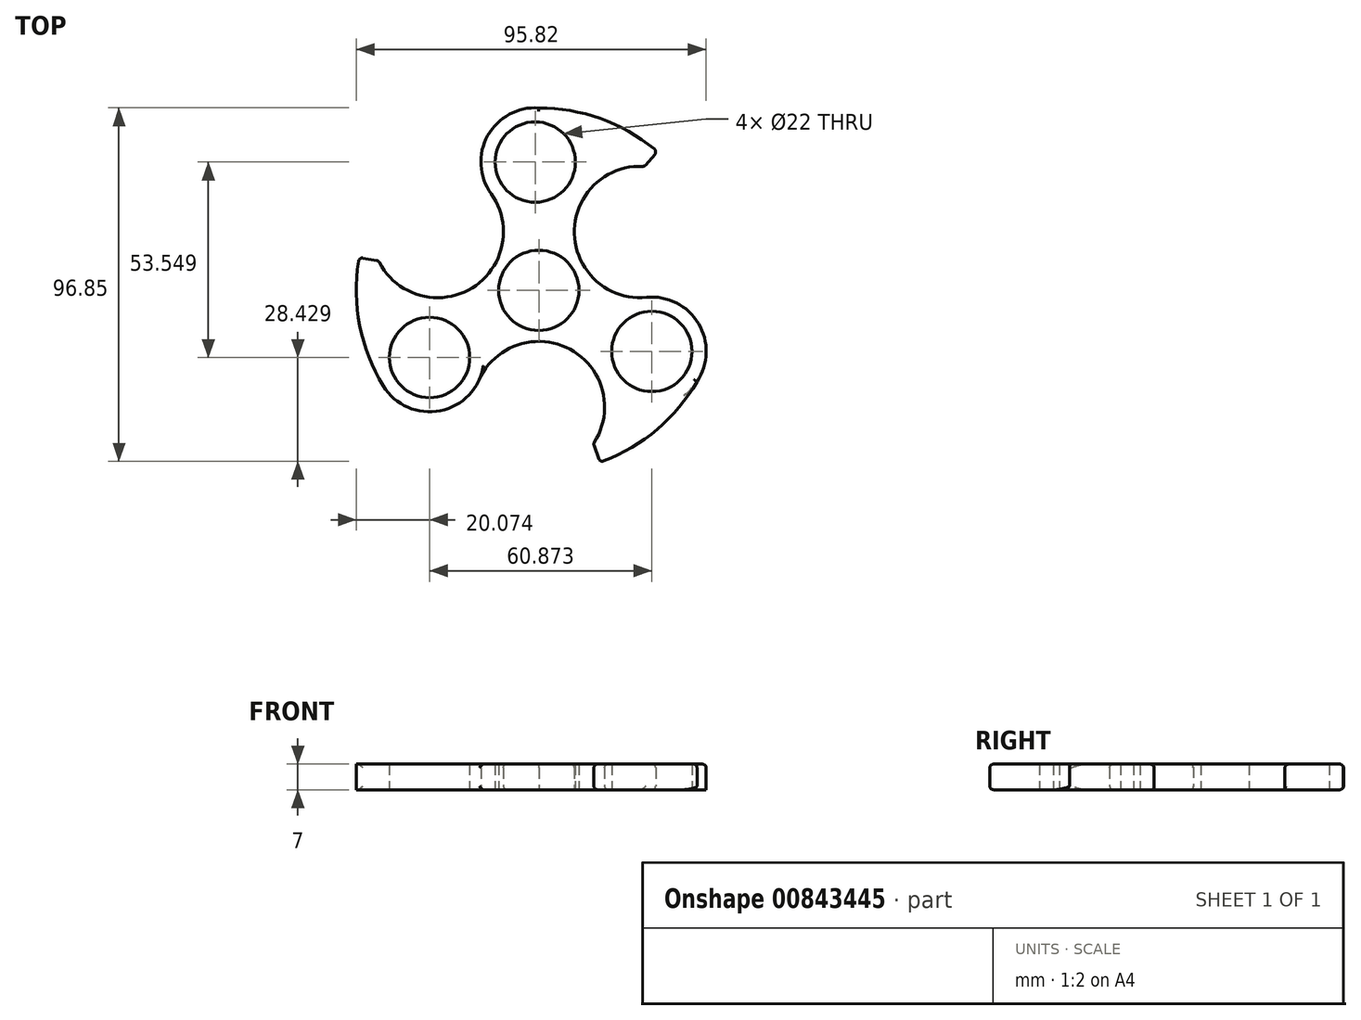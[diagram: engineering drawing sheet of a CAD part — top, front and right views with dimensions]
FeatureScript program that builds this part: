
annotation { "Feature Type Name" : "Feature", "Feature Type Description" : "" }
export const myFeature = defineFeature(function(context is Context, id is Id, definition is map)
    precondition{}
    {
        {
            var Q0;
            Q0=qCreatedBy(makeId("Top.planeOp"),FACE);
            var sketch = newSketch(context, id + "F0", { "sketchPlane" : qUnion([Q0])});
            skCircle(sketch, "E0", {"center": v(0, 0) * mm, "radius": 11 * mm});
            skArc(sketch, "E1", {"start": v(-49.18, 9.03) * mm, "mid": v(-49.15, -9.18) * mm, "end": v(-42.6, -26.18) * mm});
            skArc(sketch, "E2", {"start": v(-43.87, 8.06) * mm, "mid": v(-18.47, 0.56) * mm, "end": v(-13.09, 26.49) * mm});
            skArc(sketch, "E3", {"start": v(28.91, 33.96) * mm, "mid": v(9.72, 15.71) * mm, "end": v(29.48, -1.91) * mm});
            skArc(sketch, "E4", {"start": v(14.95, -42.02) * mm, "mid": v(8.77, -16.28) * mm, "end": v(-16.38, -24.53) * mm});
            skArc(sketch, "E5.trimOffspring", {"start": v(16.76, -47.1) * mm, "mid": v(32, -38.42) * mm, "end": v(43.3, -25) * mm});
            skArc(sketch, "E6.trimOffspring", {"start": v(32.41, 38.07) * mm, "mid": v(17.27, 46.92) * mm, "end": v(0, 50) * mm});
            skPoint(sketch, "E7", {"position": v(23.2, 38.55) * mm});
            skPoint(sketch, "E8", {"position": v(21.79, -39.38) * mm});
            skPoint(sketch, "E9", {"position": v(-45, 0.82) * mm});
            skArc(sketch, "E10", {"start": v(-13.09, 26.49) * mm, "mid": v(-14, 42.4) * mm, "end": v(0, 50) * mm});
            skArc(sketch, "E11", {"start": v(-42.6, -26.18) * mm, "mid": v(-29, -33.24) * mm, "end": v(-16.38, -24.53) * mm});
            skArc(sketch, "E12", {"start": v(29.48, -1.91) * mm, "mid": v(43.71, -9.08) * mm, "end": v(43.3, -25) * mm});
            skCircle(sketch, "E13", {"center": v(-29.93, -18.4) * mm, "radius": 11 * mm});
            skCircle(sketch, "E14", {"center": v(-1, 35.16) * mm, "radius": 11 * mm});
            skCircle(sketch, "E15", {"center": v(30.95, -16.72) * mm, "radius": 11 * mm});
            skLineSegment(sketch, "E16", {"start": v(0, 0) * mm, "end": v(37.87, 44.49) * mm, "construction": true});
            skLineSegment(sketch, "E17.1.0", {"start": v(0, 0) * mm, "end": v(-57.46, 10.56) * mm, "construction": true});
            skLineSegment(sketch, "E17.2.0", {"start": v(0, 0) * mm, "end": v(19.59, -55.04) * mm, "construction": true});
            skLineSegment(sketch, "E18", {"start": v(-49.18, 9.03) * mm, "end": v(-43.87, 8.06) * mm});
            skLineSegment(sketch, "E19", {"start": v(14.95, -42.02) * mm, "end": v(16.76, -47.1) * mm});
            skLineSegment(sketch, "E20", {"start": v(32.41, 38.07) * mm, "end": v(28.91, 33.96) * mm});
            skSolve(sketch);
        }
        {
            var Q0;
            {var subQ1=sQuery(id+"F0.wireOp",EDGE,"3f7bc842-8467-49ac-8440-9adaad4e2810.2");Q0=makeQuery(id+"F0.imprint","IMPRINT",FACE,{"disambiguationData":[TD([[makeQuery(id+"F0.imprint","IMPRINT",EDGE,{"derivedFrom":subQ1}),1.0]])]});}
            var Q1;
            {var subQ5=sQuery(id+"F0.wireOp",EDGE,"3f7bc842-8467-49ac-8440-9adaad4e2810.0");Q1=makeQuery(id+"F0.imprint","IMPRINT",FACE,{"disambiguationData":[TD([[makeQuery(id+"F0.imprint","IMPRINT",EDGE,{"derivedFrom":subQ5}),1.0]])]});}
            var Q2;
            {var subQ0=sQuery(id+"F0.wireOp",EDGE,"3f7bc842-8467-49ac-8440-9adaad4e2810.1");var subQ1=sQuery(id+"F0.wireOp",EDGE,"nu7MbhjY-MAc7-rPjX-g1DX-lD3kLk05fhsn");var subQ2=makeQuery(id+"F0.imprint","INTERSECT",VERTEX,{"derivedFrom":[subQ1,subQ0]});Q2=makeQuery(id+"F0.imprint","IMPRINT",FACE,{"disambiguationData":[TD([[makeQuery(id+"F0.imprint","IMPRINT",EDGE,{"disambiguationData":[TD([[subQ2,1.0]])],"derivedFrom":subQ0}),1.0]])]});}
            var Q3;
            {var subQ0=sQuery(id+"F0.wireOp",EDGE,"3f7bc842-8467-49ac-8440-9adaad4e2810.1");var subQ1=sQuery(id+"F0.wireOp",EDGE,"nu7MbhjY-MAc7-rPjX-g1DX-lD3kLk05fhsn");var subQ2=makeQuery(id+"F0.imprint","INTERSECT",VERTEX,{"derivedFrom":[subQ1,subQ0]});Q3=makeQuery(id+"F0.imprint","IMPRINT",FACE,{"disambiguationData":[TD([[makeQuery(id+"F0.imprint","IMPRINT",EDGE,{"disambiguationData":[TD([[subQ2,-1.0]])],"derivedFrom":subQ0}),1.0]])]});}
            var Q4;
            {var subQ0=sQuery(id+"F0.wireOp",EDGE,"E2");var subQ1=sQuery(id+"F0.wireOp",EDGE,"sv7fbsnc-qcye-DYNE-iSqw-857IQjWxAevf");var subQ2=makeQuery(id+"F0.imprint","INTERSECT",VERTEX,{"derivedFrom":[subQ1,subQ0]});Q4=makeQuery(id+"F0.imprint","IMPRINT",FACE,{"disambiguationData":[TD([[makeQuery(id+"F0.imprint","IMPRINT",EDGE,{"disambiguationData":[TD([[subQ2,-1.0]])],"derivedFrom":subQ1}),-1.0]])]});}
            var Q5;
            {var subQ0=sQuery(id+"F0.wireOp",EDGE,"E3");var subQ1=sQuery(id+"F0.wireOp",EDGE,"sv7fbsnc-qcye-DYNE-iSqw-857IQjWxAevf");var subQ2=makeQuery(id+"F0.imprint","INTERSECT",VERTEX,{"derivedFrom":[subQ1,subQ0]});Q5=makeQuery(id+"F0.imprint","IMPRINT",FACE,{"disambiguationData":[TD([[makeQuery(id+"F0.imprint","IMPRINT",EDGE,{"disambiguationData":[TD([[subQ2,1.0]])],"derivedFrom":subQ1}),-1.0]])]});}
            var Q6;
            {var subQ3=sQuery(id+"F0.wireOp",EDGE,"E2");var subQ5=sQuery(id+"F0.wireOp",EDGE,"C4j8nSnC-YMSu-Lszk-EYxg-b8w5SDZCJpY5");var subQ6=makeQuery(id+"F0.imprint","INTERSECT",VERTEX,{"disambiguationData":[OD(0.0)],"derivedFrom":[subQ5,subQ3]});Q6=makeQuery(id+"F0.imprint","IMPRINT",FACE,{"disambiguationData":[TD([[makeQuery(id+"F0.imprint","IMPRINT",EDGE,{"disambiguationData":[TD([[subQ6,1.0]])],"derivedFrom":subQ5}),1.0]])]});}
            var Q7;
            {var subQ1=sQuery(id+"F0.wireOp",EDGE,"C4j8nSnC-YMSu-Lszk-EYxg-b8w5SDZCJpY5");var subQ7=sQuery(id+"F0.wireOp",EDGE,"E3");var subQ9=makeQuery(id+"F0.imprint","INTERSECT",VERTEX,{"disambiguationData":[OD(1.0)],"derivedFrom":[subQ1,subQ7]});Q7=makeQuery(id+"F0.imprint","IMPRINT",FACE,{"disambiguationData":[TD([[makeQuery(id+"F0.imprint","IMPRINT",EDGE,{"disambiguationData":[TD([[subQ9,-1.0]])],"derivedFrom":subQ1}),1.0]])]});}
            var Q8;
            {var subQ1=sQuery(id+"F0.wireOp",EDGE,"C4j8nSnC-YMSu-Lszk-EYxg-b8w5SDZCJpY5");var subQ5=sQuery(id+"F0.wireOp",EDGE,"E2");var subQ6=makeQuery(id+"F0.imprint","INTERSECT",VERTEX,{"disambiguationData":[OD(1.0)],"derivedFrom":[subQ1,subQ5]});Q8=makeQuery(id+"F0.imprint","IMPRINT",FACE,{"disambiguationData":[TD([[makeQuery(id+"F0.imprint","IMPRINT",EDGE,{"disambiguationData":[TD([[subQ6,-1.0]])],"derivedFrom":subQ1}),1.0]])]});}
            var Q9;
            {var subQ1=sQuery(id+"F0.wireOp",EDGE,"C4j8nSnC-YMSu-Lszk-EYxg-b8w5SDZCJpY5");var subQ5=sQuery(id+"F0.wireOp",EDGE,"E4");var subQ6=makeQuery(id+"F0.imprint","INTERSECT",VERTEX,{"disambiguationData":[OD(0.0)],"derivedFrom":[subQ1,subQ5]});Q9=makeQuery(id+"F0.imprint","IMPRINT",FACE,{"disambiguationData":[TD([[makeQuery(id+"F0.imprint","IMPRINT",EDGE,{"disambiguationData":[TD([[subQ6,1.0]])],"derivedFrom":subQ1}),1.0]])]});}
            var Q10;
            {var subQ5=sQuery(id+"F0.wireOp",EDGE,"9VgUR1kC-HbJB-ABtG-h0EX-FUHrEpssJFZg");var subQ6=sQuery(id+"F0.wireOp",EDGE,"E0");var subQ7=makeQuery(id+"F0.imprint","INTERSECT",VERTEX,{"derivedFrom":[subQ6,subQ5]});Q10=makeQuery(id+"F0.imprint","IMPRINT",FACE,{"disambiguationData":[TD([[makeQuery(id+"F0.imprint","IMPRINT",EDGE,{"disambiguationData":[TD([[subQ7,-1.0]])],"derivedFrom":subQ6}),-1.0]])]});}
            var Q11;
            {var subQ1=sQuery(id+"F0.wireOp",EDGE,"E0");var subQ9=sQuery(id+"F0.wireOp",EDGE,"CFaMabJv-BaBl-nt57-wO3A-6JOnLyDZJUd2");var subQ11=makeQuery(id+"F0.imprint","INTERSECT",VERTEX,{"derivedFrom":[subQ1,subQ9]});Q11=makeQuery(id+"F0.imprint","IMPRINT",FACE,{"disambiguationData":[TD([[makeQuery(id+"F0.imprint","IMPRINT",EDGE,{"disambiguationData":[TD([[subQ11,1.0]])],"derivedFrom":subQ1}),-1.0]])]});}
            var Q12;
            {var subQ0=sQuery(id+"F0.wireOp",EDGE,"E3");var subQ1=sQuery(id+"F0.wireOp",EDGE,"x40MpVTq-PCuQ-1TBw-DNN8-5xuqoy8G5yz2");var subQ2=makeQuery(id+"F0.imprint","INTERSECT",VERTEX,{"derivedFrom":[subQ1,subQ0]});Q12=makeQuery(id+"F0.imprint","IMPRINT",FACE,{"disambiguationData":[TD([[makeQuery(id+"F0.imprint","IMPRINT",EDGE,{"disambiguationData":[TD([[subQ2,-1.0]])],"derivedFrom":subQ1}),-1.0]])]});}
            var Q13;
            {var subQ0=sQuery(id+"F0.wireOp",EDGE,"E4");var subQ1=sQuery(id+"F0.wireOp",EDGE,"x40MpVTq-PCuQ-1TBw-DNN8-5xuqoy8G5yz2");var subQ2=makeQuery(id+"F0.imprint","INTERSECT",VERTEX,{"derivedFrom":[subQ1,subQ0]});Q13=makeQuery(id+"F0.imprint","IMPRINT",FACE,{"disambiguationData":[TD([[makeQuery(id+"F0.imprint","IMPRINT",EDGE,{"disambiguationData":[TD([[subQ2,1.0]])],"derivedFrom":subQ1}),-1.0]])]});}
            var Q14;
            {var subQ0=sQuery(id+"F0.wireOp",EDGE,"49722dc7-dc7b-4ebf-b22a-0d9910023828.2");Q14=makeQuery(id+"F0.imprint","IMPRINT",FACE,{"disambiguationData":[TD([[makeQuery(id+"F0.imprint","IMPRINT",EDGE,{"derivedFrom":subQ0}),1.0]])]});}
            var Q15;
            {var subQ5=sQuery(id+"F0.wireOp",EDGE,"49722dc7-dc7b-4ebf-b22a-0d9910023828.0");Q15=makeQuery(id+"F0.imprint","IMPRINT",FACE,{"disambiguationData":[TD([[makeQuery(id+"F0.imprint","IMPRINT",EDGE,{"derivedFrom":subQ5}),1.0]])]});}
            var Q16;
            {var subQ0=sQuery(id+"F0.wireOp",EDGE,"E5.trimOffspring");Q16=makeQuery(id+"F0.imprint","IMPRINT",FACE,{"disambiguationData":[TD([[makeQuery(id+"F0.imprint","IMPRINT",EDGE,{"derivedFrom":subQ0}),1.0]])]});}
            var Q17;
            {var subQ0=sQuery(id+"F0.wireOp",EDGE,"49722dc7-dc7b-4ebf-b22a-0d9910023828.4");var subQ1=sQuery(id+"F0.wireOp",EDGE,"88UstpRX-54K3-uVYN-JsYc-c1O7LK7eOc8f");var subQ2=makeQuery(id+"F0.imprint","INTERSECT",VERTEX,{"derivedFrom":[subQ1,subQ0]});Q17=makeQuery(id+"F0.imprint","IMPRINT",FACE,{"disambiguationData":[TD([[makeQuery(id+"F0.imprint","IMPRINT",EDGE,{"disambiguationData":[TD([[subQ2,1.0]])],"derivedFrom":subQ0}),1.0]])]});}
            var Q18;
            {var subQ0=sQuery(id+"F0.wireOp",EDGE,"49722dc7-dc7b-4ebf-b22a-0d9910023828.4");var subQ1=sQuery(id+"F0.wireOp",EDGE,"88UstpRX-54K3-uVYN-JsYc-c1O7LK7eOc8f");var subQ2=makeQuery(id+"F0.imprint","INTERSECT",VERTEX,{"derivedFrom":[subQ1,subQ0]});Q18=makeQuery(id+"F0.imprint","IMPRINT",FACE,{"disambiguationData":[TD([[makeQuery(id+"F0.imprint","IMPRINT",EDGE,{"disambiguationData":[TD([[subQ2,-1.0]])],"derivedFrom":subQ0}),1.0]])]});}
            var Q19;
            {var subQ0=sQuery(id+"F0.wireOp",EDGE,"E6.trimOffspring");Q19=makeQuery(id+"F0.imprint","IMPRINT",FACE,{"disambiguationData":[TD([[makeQuery(id+"F0.imprint","IMPRINT",EDGE,{"derivedFrom":subQ0}),1.0]])]});}
            var Q20;
            {var subQ0=sQuery(id+"F0.wireOp",EDGE,"4Rxz6dJ8-GsAv-ijvN-txGC-AziJ4LwzvlZd");var subQ1=sQuery(id+"F0.wireOp",EDGE,"sv7fbsnc-qcye-DYNE-iSqw-857IQjWxAevf");var subQ2=makeQuery(id+"F0.imprint","INTERSECT",VERTEX,{"disambiguationData":[OD(0.0)],"derivedFrom":[subQ1,subQ0]});Q20=makeQuery(id+"F0.imprint","IMPRINT",FACE,{"disambiguationData":[TD([[makeQuery(id+"F0.imprint","IMPRINT",EDGE,{"disambiguationData":[TD([[subQ2,-1.0]])],"derivedFrom":subQ0}),1.0]])]});}
            var Q21;
            {var subQ0=sQuery(id+"F0.wireOp",EDGE,"4Rxz6dJ8-GsAv-ijvN-txGC-AziJ4LwzvlZd");var subQ1=sQuery(id+"F0.wireOp",EDGE,"sv7fbsnc-qcye-DYNE-iSqw-857IQjWxAevf");var subQ2=makeQuery(id+"F0.imprint","INTERSECT",VERTEX,{"disambiguationData":[OD(1.0)],"derivedFrom":[subQ1,subQ0]});Q21=makeQuery(id+"F0.imprint","IMPRINT",FACE,{"disambiguationData":[TD([[makeQuery(id+"F0.imprint","IMPRINT",EDGE,{"disambiguationData":[TD([[subQ2,1.0]])],"derivedFrom":subQ0}),1.0]])]});}
            var Q22;
            {var subQ0=sQuery(id+"F0.wireOp",EDGE,"4Rxz6dJ8-GsAv-ijvN-txGC-AziJ4LwzvlZd");var subQ3=sQuery(id+"F0.wireOp",EDGE,"C4j8nSnC-YMSu-Lszk-EYxg-b8w5SDZCJpY5");var subQ5=makeQuery(id+"F0.imprint","INTERSECT",VERTEX,{"disambiguationData":[OD(0.0)],"derivedFrom":[subQ3,subQ0]});Q22=makeQuery(id+"F0.imprint","IMPRINT",FACE,{"disambiguationData":[TD([[makeQuery(id+"F0.imprint","IMPRINT",EDGE,{"disambiguationData":[TD([[subQ5,-1.0]])],"derivedFrom":subQ3}),1.0]])]});}
            var Q23;
            {var subQ0=sQuery(id+"F0.wireOp",EDGE,"4Rxz6dJ8-GsAv-ijvN-txGC-AziJ4LwzvlZd");var subQ3=sQuery(id+"F0.wireOp",EDGE,"C4j8nSnC-YMSu-Lszk-EYxg-b8w5SDZCJpY5");var subQ5=makeQuery(id+"F0.imprint","INTERSECT",VERTEX,{"disambiguationData":[OD(1.0)],"derivedFrom":[subQ3,subQ0]});Q23=makeQuery(id+"F0.imprint","IMPRINT",FACE,{"disambiguationData":[TD([[makeQuery(id+"F0.imprint","IMPRINT",EDGE,{"disambiguationData":[TD([[subQ5,1.0]])],"derivedFrom":subQ3}),1.0]])]});}
            var Q24;
            {var subQ0=sQuery(id+"F0.wireOp",EDGE,"gMAYUmRH-FaYY-2lfT-oHka-ojM136KSUSHD");var subQ1=sQuery(id+"F0.wireOp",EDGE,"88UstpRX-54K3-uVYN-JsYc-c1O7LK7eOc8f");var subQ2=makeQuery(id+"F0.imprint","INTERSECT",VERTEX,{"disambiguationData":[OD(0.0)],"derivedFrom":[subQ1,subQ0]});Q24=makeQuery(id+"F0.imprint","IMPRINT",FACE,{"disambiguationData":[TD([[makeQuery(id+"F0.imprint","IMPRINT",EDGE,{"disambiguationData":[TD([[subQ2,-1.0]])],"derivedFrom":subQ1}),1.0]])]});}
            var Q25;
            {var subQ0=sQuery(id+"F0.wireOp",EDGE,"gMAYUmRH-FaYY-2lfT-oHka-ojM136KSUSHD");var subQ1=sQuery(id+"F0.wireOp",EDGE,"88UstpRX-54K3-uVYN-JsYc-c1O7LK7eOc8f");var subQ2=makeQuery(id+"F0.imprint","INTERSECT",VERTEX,{"disambiguationData":[OD(0.0)],"derivedFrom":[subQ1,subQ0]});Q25=makeQuery(id+"F0.imprint","IMPRINT",FACE,{"disambiguationData":[TD([[makeQuery(id+"F0.imprint","IMPRINT",EDGE,{"disambiguationData":[TD([[subQ2,-1.0]])],"derivedFrom":subQ1}),-1.0]])]});}
            var Q26;
            {var subQ1=sQuery(id+"F0.wireOp",EDGE,"88UstpRX-54K3-uVYN-JsYc-c1O7LK7eOc8f");var subQ5=sQuery(id+"F0.wireOp",EDGE,"C4j8nSnC-YMSu-Lszk-EYxg-b8w5SDZCJpY5");var subQ6=makeQuery(id+"F0.imprint","INTERSECT",VERTEX,{"derivedFrom":[subQ1,subQ5]});Q26=makeQuery(id+"F0.imprint","IMPRINT",FACE,{"disambiguationData":[TD([[makeQuery(id+"F0.imprint","IMPRINT",EDGE,{"disambiguationData":[TD([[subQ6,-1.0]])],"derivedFrom":subQ1}),-1.0]])]});}
            var Q27;
            {var subQ1=sQuery(id+"F0.wireOp",EDGE,"88UstpRX-54K3-uVYN-JsYc-c1O7LK7eOc8f");var subQ7=sQuery(id+"F0.wireOp",EDGE,"C4j8nSnC-YMSu-Lszk-EYxg-b8w5SDZCJpY5");var subQ8=makeQuery(id+"F0.imprint","INTERSECT",VERTEX,{"derivedFrom":[subQ1,subQ7]});Q27=makeQuery(id+"F0.imprint","IMPRINT",FACE,{"disambiguationData":[TD([[makeQuery(id+"F0.imprint","IMPRINT",EDGE,{"disambiguationData":[TD([[subQ8,-1.0]])],"derivedFrom":subQ1}),1.0]])]});}
            var Q28;
            {var subQ0=sQuery(id+"F0.wireOp",EDGE,"E1");Q28=makeQuery(id+"F0.imprint","IMPRINT",FACE,{"disambiguationData":[TD([[makeQuery(id+"F0.imprint","IMPRINT",EDGE,{"derivedFrom":subQ0}),1.0]])]});}
            var Q29;
            {var subQ1=sQuery(id+"F0.wireOp",EDGE,"d8093a5b-4d6d-4e08-b9a8-8a5bac8dbfa5.3");Q29=makeQuery(id+"F0.imprint","IMPRINT",FACE,{"disambiguationData":[TD([[makeQuery(id+"F0.imprint","IMPRINT",EDGE,{"derivedFrom":subQ1}),1.0]])]});}
            var Q30;
            {var subQ4=sQuery(id+"F0.wireOp",EDGE,"d8093a5b-4d6d-4e08-b9a8-8a5bac8dbfa5.0");Q30=makeQuery(id+"F0.imprint","IMPRINT",FACE,{"disambiguationData":[TD([[makeQuery(id+"F0.imprint","IMPRINT",EDGE,{"derivedFrom":subQ4}),1.0]])]});}
            var Q31;
            {var subQ0=sQuery(id+"F0.wireOp",EDGE,"E4");var subQ1=sQuery(id+"F0.wireOp",EDGE,"RUABtInU-iKBV-EQpS-h9ne-nRwwB5inRPBh");var subQ2=makeQuery(id+"F0.imprint","INTERSECT",VERTEX,{"derivedFrom":[subQ1,subQ0]});Q31=makeQuery(id+"F0.imprint","IMPRINT",FACE,{"disambiguationData":[TD([[makeQuery(id+"F0.imprint","IMPRINT",EDGE,{"disambiguationData":[TD([[subQ2,-1.0]])],"derivedFrom":subQ1}),-1.0]])]});}
            var Q32;
            {var subQ0=sQuery(id+"F0.wireOp",EDGE,"E2");var subQ1=sQuery(id+"F0.wireOp",EDGE,"RUABtInU-iKBV-EQpS-h9ne-nRwwB5inRPBh");var subQ2=makeQuery(id+"F0.imprint","INTERSECT",VERTEX,{"derivedFrom":[subQ1,subQ0]});Q32=makeQuery(id+"F0.imprint","IMPRINT",FACE,{"disambiguationData":[TD([[makeQuery(id+"F0.imprint","IMPRINT",EDGE,{"disambiguationData":[TD([[subQ2,1.0]])],"derivedFrom":subQ1}),-1.0]])]});}
            var Q33;
            {var subQ0=sQuery(id+"F0.wireOp",EDGE,"d8093a5b-4d6d-4e08-b9a8-8a5bac8dbfa5.5");var subQ1=sQuery(id+"F0.wireOp",EDGE,"mKOXe6AH-uMiB-TUgd-KZ6j-uo9zpwvRpa4S");var subQ2=makeQuery(id+"F0.imprint","INTERSECT",VERTEX,{"derivedFrom":[subQ1,subQ0]});Q33=makeQuery(id+"F0.imprint","IMPRINT",FACE,{"disambiguationData":[TD([[makeQuery(id+"F0.imprint","IMPRINT",EDGE,{"disambiguationData":[TD([[subQ2,-1.0]])],"derivedFrom":subQ0}),1.0]])]});}
            var Q34;
            {var subQ0=sQuery(id+"F0.wireOp",EDGE,"d8093a5b-4d6d-4e08-b9a8-8a5bac8dbfa5.5");var subQ1=sQuery(id+"F0.wireOp",EDGE,"mKOXe6AH-uMiB-TUgd-KZ6j-uo9zpwvRpa4S");var subQ2=makeQuery(id+"F0.imprint","INTERSECT",VERTEX,{"derivedFrom":[subQ1,subQ0]});Q34=makeQuery(id+"F0.imprint","IMPRINT",FACE,{"disambiguationData":[TD([[makeQuery(id+"F0.imprint","IMPRINT",EDGE,{"disambiguationData":[TD([[subQ2,1.0]])],"derivedFrom":subQ0}),1.0]])]});}
            var Q35;
            {var subQ0=sQuery(id+"F0.wireOp",EDGE,"kEFfzBxr-I8kb-SGwx-hxRS-iwMc0eVOOg4E");var subQ1=sQuery(id+"F0.wireOp",EDGE,"RUABtInU-iKBV-EQpS-h9ne-nRwwB5inRPBh");var subQ2=makeQuery(id+"F0.imprint","INTERSECT",VERTEX,{"disambiguationData":[OD(1.0)],"derivedFrom":[subQ1,subQ0]});Q35=makeQuery(id+"F0.imprint","IMPRINT",FACE,{"disambiguationData":[TD([[makeQuery(id+"F0.imprint","IMPRINT",EDGE,{"disambiguationData":[TD([[subQ2,1.0]])],"derivedFrom":subQ0}),1.0]])]});}
            var Q36;
            {var subQ0=sQuery(id+"F0.wireOp",EDGE,"kEFfzBxr-I8kb-SGwx-hxRS-iwMc0eVOOg4E");var subQ1=sQuery(id+"F0.wireOp",EDGE,"RUABtInU-iKBV-EQpS-h9ne-nRwwB5inRPBh");var subQ2=makeQuery(id+"F0.imprint","INTERSECT",VERTEX,{"disambiguationData":[OD(0.0)],"derivedFrom":[subQ1,subQ0]});Q36=makeQuery(id+"F0.imprint","IMPRINT",FACE,{"disambiguationData":[TD([[makeQuery(id+"F0.imprint","IMPRINT",EDGE,{"disambiguationData":[TD([[subQ2,-1.0]])],"derivedFrom":subQ0}),1.0]])]});}
            var Q37;
            {var subQ0=sQuery(id+"F0.wireOp",EDGE,"kEFfzBxr-I8kb-SGwx-hxRS-iwMc0eVOOg4E");var subQ3=sQuery(id+"F0.wireOp",EDGE,"C4j8nSnC-YMSu-Lszk-EYxg-b8w5SDZCJpY5");var subQ5=makeQuery(id+"F0.imprint","INTERSECT",VERTEX,{"disambiguationData":[OD(1.0)],"derivedFrom":[subQ3,subQ0]});Q37=makeQuery(id+"F0.imprint","IMPRINT",FACE,{"disambiguationData":[TD([[makeQuery(id+"F0.imprint","IMPRINT",EDGE,{"disambiguationData":[TD([[subQ5,1.0]])],"derivedFrom":subQ3}),1.0]])]});}
            var Q38;
            {var subQ0=sQuery(id+"F0.wireOp",EDGE,"kEFfzBxr-I8kb-SGwx-hxRS-iwMc0eVOOg4E");var subQ3=sQuery(id+"F0.wireOp",EDGE,"C4j8nSnC-YMSu-Lszk-EYxg-b8w5SDZCJpY5");var subQ5=makeQuery(id+"F0.imprint","INTERSECT",VERTEX,{"disambiguationData":[OD(0.0)],"derivedFrom":[subQ3,subQ0]});Q38=makeQuery(id+"F0.imprint","IMPRINT",FACE,{"disambiguationData":[TD([[makeQuery(id+"F0.imprint","IMPRINT",EDGE,{"disambiguationData":[TD([[subQ5,-1.0]])],"derivedFrom":subQ3}),1.0]])]});}
            var Q39;
            {var subQ0=sQuery(id+"F0.wireOp",EDGE,"DQ5kVecW-1MrT-lyVf-wv95-HuLgpyEHOht9");var subQ1=sQuery(id+"F0.wireOp",EDGE,"C4j8nSnC-YMSu-Lszk-EYxg-b8w5SDZCJpY5");var subQ2=makeQuery(id+"F0.imprint","INTERSECT",VERTEX,{"derivedFrom":[subQ1,subQ0]});Q39=makeQuery(id+"F0.imprint","IMPRINT",FACE,{"disambiguationData":[TD([[makeQuery(id+"F0.imprint","IMPRINT",EDGE,{"disambiguationData":[TD([[subQ2,-1.0]])],"derivedFrom":subQ1}),1.0]])]});}
            var Q40;
            {var subQ0=sQuery(id+"F0.wireOp",EDGE,"DQ5kVecW-1MrT-lyVf-wv95-HuLgpyEHOht9");var subQ1=sQuery(id+"F0.wireOp",EDGE,"C4j8nSnC-YMSu-Lszk-EYxg-b8w5SDZCJpY5");var subQ2=makeQuery(id+"F0.imprint","INTERSECT",VERTEX,{"derivedFrom":[subQ1,subQ0]});Q40=makeQuery(id+"F0.imprint","IMPRINT",FACE,{"disambiguationData":[TD([[makeQuery(id+"F0.imprint","IMPRINT",EDGE,{"disambiguationData":[TD([[subQ2,1.0]])],"derivedFrom":subQ1}),1.0]])]});}
            var Q41;
            {var subQ0=sQuery(id+"F0.wireOp",EDGE,"CFaMabJv-BaBl-nt57-wO3A-6JOnLyDZJUd2");var subQ1=sQuery(id+"F0.wireOp",EDGE,"C4j8nSnC-YMSu-Lszk-EYxg-b8w5SDZCJpY5");var subQ2=makeQuery(id+"F0.imprint","INTERSECT",VERTEX,{"derivedFrom":[subQ1,subQ0]});Q41=makeQuery(id+"F0.imprint","IMPRINT",FACE,{"disambiguationData":[TD([[makeQuery(id+"F0.imprint","IMPRINT",EDGE,{"disambiguationData":[TD([[subQ2,-1.0]])],"derivedFrom":subQ1}),1.0]])]});}
            var Q42;
            {var subQ0=sQuery(id+"F0.wireOp",EDGE,"CFaMabJv-BaBl-nt57-wO3A-6JOnLyDZJUd2");var subQ1=sQuery(id+"F0.wireOp",EDGE,"C4j8nSnC-YMSu-Lszk-EYxg-b8w5SDZCJpY5");var subQ2=makeQuery(id+"F0.imprint","INTERSECT",VERTEX,{"derivedFrom":[subQ1,subQ0]});Q42=makeQuery(id+"F0.imprint","IMPRINT",FACE,{"disambiguationData":[TD([[makeQuery(id+"F0.imprint","IMPRINT",EDGE,{"disambiguationData":[TD([[subQ2,1.0]])],"derivedFrom":subQ1}),1.0]])]});}
            var Q43;
            {var subQ0=sQuery(id+"F0.wireOp",EDGE,"9VgUR1kC-HbJB-ABtG-h0EX-FUHrEpssJFZg");var subQ1=sQuery(id+"F0.wireOp",EDGE,"C4j8nSnC-YMSu-Lszk-EYxg-b8w5SDZCJpY5");var subQ2=makeQuery(id+"F0.imprint","INTERSECT",VERTEX,{"derivedFrom":[subQ1,subQ0]});Q43=makeQuery(id+"F0.imprint","IMPRINT",FACE,{"disambiguationData":[TD([[makeQuery(id+"F0.imprint","IMPRINT",EDGE,{"disambiguationData":[TD([[subQ2,-1.0]])],"derivedFrom":subQ1}),1.0]])]});}
            var Q44;
            {var subQ0=sQuery(id+"F0.wireOp",EDGE,"9VgUR1kC-HbJB-ABtG-h0EX-FUHrEpssJFZg");var subQ1=sQuery(id+"F0.wireOp",EDGE,"C4j8nSnC-YMSu-Lszk-EYxg-b8w5SDZCJpY5");var subQ2=makeQuery(id+"F0.imprint","INTERSECT",VERTEX,{"derivedFrom":[subQ1,subQ0]});Q44=makeQuery(id+"F0.imprint","IMPRINT",FACE,{"disambiguationData":[TD([[makeQuery(id+"F0.imprint","IMPRINT",EDGE,{"disambiguationData":[TD([[subQ2,1.0]])],"derivedFrom":subQ1}),1.0]])]});}
            extrude(context, id + "F1", {"entities" : qUnion([Q0, Q1, Q2, Q3, Q4, Q5, Q6, Q7, Q8, Q9, Q10, Q11, Q12, Q13, Q14, Q15, Q16, Q17, Q18, Q19, Q20, Q21, Q22, Q23, Q24, Q25, Q26, Q27, Q28, Q29, Q30, Q31, Q32, Q33, Q34, Q35, Q36, Q37, Q38, Q39, Q40, Q41, Q42, Q43, Q44]), "depth" : 7 * mm, "offsetDistance" : 25 * mm});
        }
        {
            var Q0;
            Q0=makeQuery(id+"F1.opExtrude","CAP_EDGE",EDGE,{"disambiguationData":[OSD([sQuery(id+"F0.wireOp",EDGE,"E2")])],"isStart":false});
            var Q1;
            Q1=makeQuery(id+"F1.opExtrude","CAP_EDGE",EDGE,{"disambiguationData":[OSD([sQuery(id+"F0.wireOp",EDGE,"E4")])],"isStart":false});
            var Q2;
            Q2=makeQuery(id+"F1.opExtrude","CAP_EDGE",EDGE,{"disambiguationData":[OSD([sQuery(id+"F0.wireOp",EDGE,"E3")])],"isStart":false});
            var Q3;
            Q3=makeQuery(id+"F1.opExtrude","CAP_EDGE",EDGE,{"disambiguationData":[OSD([sQuery(id+"F0.wireOp",EDGE,"E10")])],"isStart":true});
            var Q4;
            Q4=makeQuery(id+"F1.opExtrude","CAP_EDGE",EDGE,{"disambiguationData":[OSD([sQuery(id+"F0.wireOp",EDGE,"E4")])],"isStart":true});
            var Q5;
            Q5=makeQuery(id+"F1.opExtrude","CAP_EDGE",EDGE,{"disambiguationData":[OSD([sQuery(id+"F0.wireOp",EDGE,"E5.trimOffspring")])],"isStart":true});
            var Q6;
            Q6=makeQuery(id+"F1.opExtrude","CAP_EDGE",EDGE,{"disambiguationData":[OSD([sQuery(id+"F0.wireOp",EDGE,"E18")])],"isStart":false});
            var Q7;
            Q7=makeQuery(id+"F1.opExtrude","CAP_EDGE",EDGE,{"disambiguationData":[OSD([sQuery(id+"F0.wireOp",EDGE,"E18")])],"isStart":true});
            var Q8;
            Q8=makeQuery(id+"F1.opExtrude","CAP_EDGE",EDGE,{"disambiguationData":[OSD([sQuery(id+"F0.wireOp",EDGE,"E19")])],"isStart":false});
            var Q9;
            Q9=makeQuery(id+"F1.opExtrude","CAP_EDGE",EDGE,{"disambiguationData":[OSD([sQuery(id+"F0.wireOp",EDGE,"E19")])],"isStart":true});
            var Q10;
            Q10=makeQuery(id+"F1.opExtrude","SWEPT_EDGE",EDGE,{"disambiguationData":[OSD([sQuery(id+"F0.wireOp",EDGE,"E4"),sQuery(id+"F0.wireOp",EDGE,"E19")])]});
            var Q11;
            Q11=makeQuery(id+"F1.opExtrude","SWEPT_EDGE",EDGE,{"disambiguationData":[OSD([sQuery(id+"F0.wireOp",EDGE,"E5.trimOffspring"),sQuery(id+"F0.wireOp",EDGE,"E19")])]});
            var Q12;
            Q12=makeQuery(id+"F1.opExtrude","SWEPT_EDGE",EDGE,{"disambiguationData":[OSD([sQuery(id+"F0.wireOp",EDGE,"E3"),sQuery(id+"F0.wireOp",EDGE,"E20")])]});
            var Q13;
            Q13=makeQuery(id+"F1.opExtrude","CAP_EDGE",EDGE,{"disambiguationData":[OSD([sQuery(id+"F0.wireOp",EDGE,"E20")])],"isStart":false});
            var Q14;
            Q14=makeQuery(id+"F1.opExtrude","SWEPT_EDGE",EDGE,{"disambiguationData":[OSD([sQuery(id+"F0.wireOp",EDGE,"E6.trimOffspring"),sQuery(id+"F0.wireOp",EDGE,"E20")])]});
            var Q15;
            Q15=makeQuery(id+"F1.opExtrude","CAP_EDGE",EDGE,{"disambiguationData":[OSD([sQuery(id+"F0.wireOp",EDGE,"E20")])],"isStart":true});
            var Q16;
            Q16=makeQuery(id+"F1.opExtrude","SWEPT_EDGE",EDGE,{"disambiguationData":[OSD([sQuery(id+"F0.wireOp",EDGE,"E2"),sQuery(id+"F0.wireOp",EDGE,"E18")])]});
            var Q17;
            Q17=makeQuery(id+"F1.opExtrude","SWEPT_EDGE",EDGE,{"disambiguationData":[OSD([sQuery(id+"F0.wireOp",EDGE,"E1"),sQuery(id+"F0.wireOp",EDGE,"E18")])]});
            fillet(context, id + "F2", {"entities" : qUnion([Q0, Q1, Q2, Q3, Q4, Q5, Q6, Q7, Q8, Q9, Q10, Q11, Q12, Q13, Q14, Q15, Q16, Q17]), "radius" : 1 * mm, "tangentPropagation" : true, "allowEdgeOverflow" : false});
        }
    });
